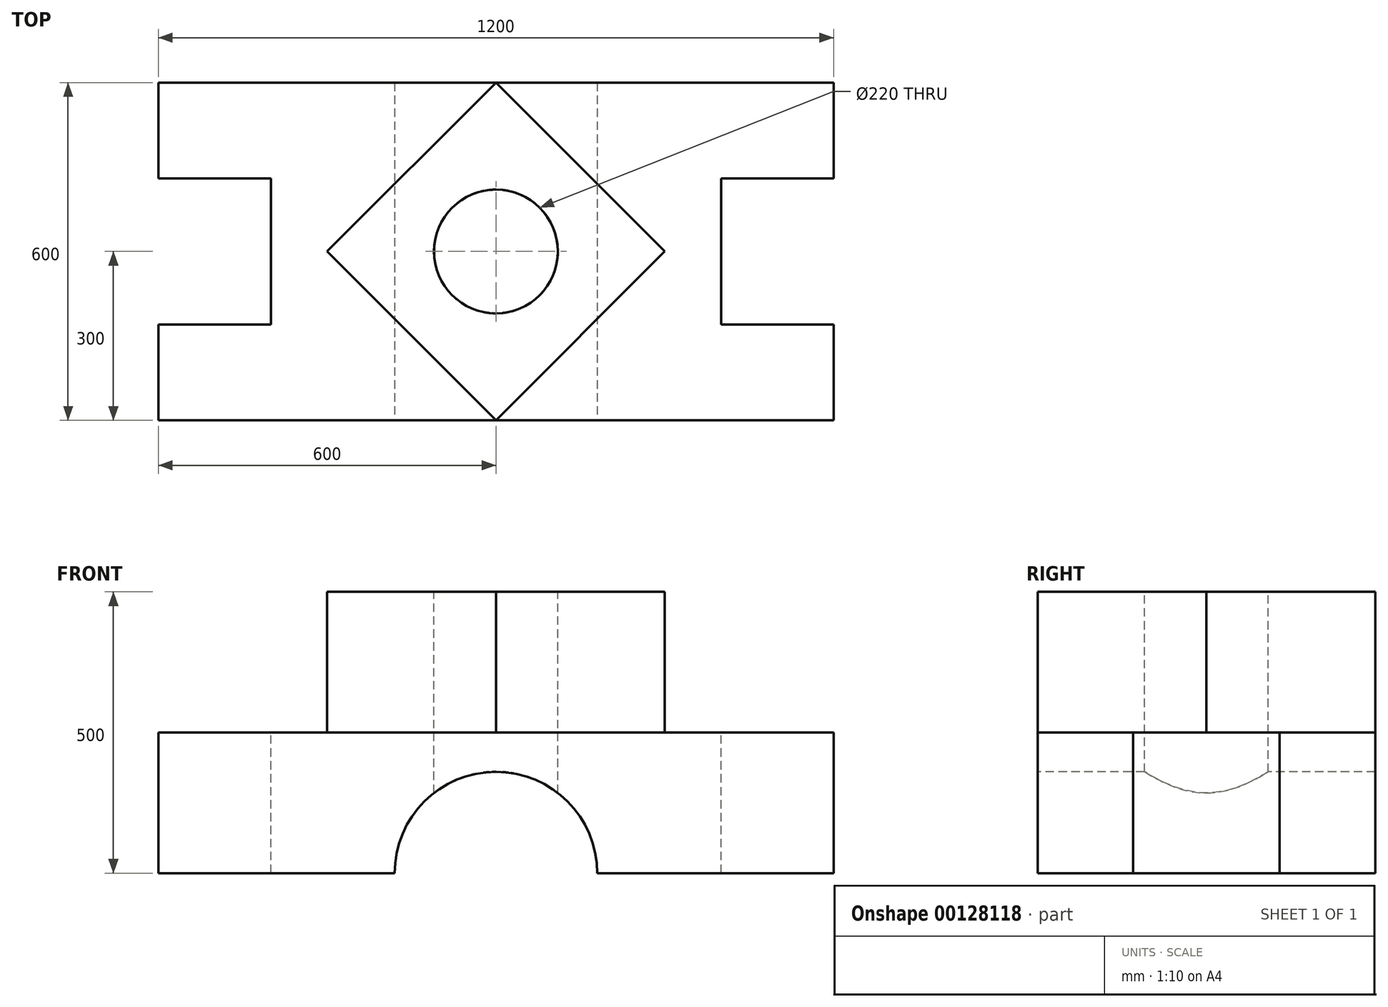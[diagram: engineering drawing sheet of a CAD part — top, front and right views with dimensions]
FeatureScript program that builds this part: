
annotation { "Feature Type Name" : "Feature", "Feature Type Description" : "" }
export const myFeature = defineFeature(function(context is Context, id is Id, definition is map)
    precondition{}
    {
        {
            var Q0;
            Q0=qCreatedBy(makeId("Top.planeOp"),FACE);
            var sketch = newSketch(context, id + "F0", { "sketchPlane" : qUnion([Q0])});
            skLineSegment(sketch, "E0.bottom", {"start": v(600, -300) * mm, "end": v(-600, -300) * mm});
            skLineSegment(sketch, "E0.top", {"start": v(600, 300) * mm, "end": v(-600, 300) * mm});
            skLineSegment(sketch, "E0.left", {"start": v(600, -300) * mm, "end": v(600, 300) * mm});
            skLineSegment(sketch, "E0.right", {"start": v(-600, -300) * mm, "end": v(-600, 300) * mm});
            skPoint(sketch, "E0.middle", {"position": v(0, 0) * mm});
            skSolve(sketch);
        }
        {
            var Q0;
            Q0 = qSketchRegion(id + "F0", true);
            extrude(context, id + "F1", {"entities" : qUnion([Q0]), "depth" : 250 * mm});
        }
        {
            var Q0;
            Q0=makeQuery(id+"F1.opExtrude","CAP_FACE",FACE,{"disambiguationData":[OSD([sQuery(id+"F0.wireOp",EDGE,"E0.bottom"),sQuery(id+"F0.wireOp",EDGE,"E0.top"),sQuery(id+"F0.wireOp",EDGE,"E0.left"),sQuery(id+"F0.wireOp",EDGE,"E0.right")])],"isStart":false});
            var sketch = newSketch(context, id + "F2", { "sketchPlane" : qUnion([Q0])});
            skPoint(sketch, "E1.middle", {"position": v(600, 0) * mm});
            skPoint(sketch, "E2.middle", {"position": v(-600, 0) * mm});
            skLineSegment(sketch, "E3.bottom", {"start": v(-400, -130) * mm, "end": v(-800, -130) * mm});
            skLineSegment(sketch, "E3.top", {"start": v(-400, 130) * mm, "end": v(-800, 130) * mm});
            skLineSegment(sketch, "E3.left", {"start": v(-400, -130) * mm, "end": v(-400, 130) * mm});
            skLineSegment(sketch, "E3.right", {"start": v(-800, -130) * mm, "end": v(-800, 130) * mm});
            skLineSegment(sketch, "E4.bottom", {"start": v(400, -130) * mm, "end": v(800, -130) * mm});
            skLineSegment(sketch, "E4.top", {"start": v(400, 130) * mm, "end": v(800, 130) * mm});
            skLineSegment(sketch, "E4.left", {"start": v(400, -130) * mm, "end": v(400, 130) * mm});
            skLineSegment(sketch, "E4.right", {"start": v(800, -130) * mm, "end": v(800, 130) * mm});
            skSolve(sketch);
        }
        {
            var Q0;
            Q0 = qSketchRegion(id + "F2", true);
            var Q1;
            {var subQ0=sQuery(id+"F2.wireOp",EDGE,"E2.bottom");Q1=makeQuery(id+"F2.imprint","IMPRINT",FACE,{"disambiguationData":[TD([[makeQuery(id+"F2.imprint","IMPRINT",EDGE,{"derivedFrom":subQ0}),-1.0]])]});}
            var Q2;
            {var subQ0=sQuery(id+"F2.wireOp",EDGE,"E1.bottom");Q2=makeQuery(id+"F2.imprint","IMPRINT",FACE,{"disambiguationData":[TD([[makeQuery(id+"F2.imprint","IMPRINT",EDGE,{"derivedFrom":subQ0}),1.0]])]});}
            extrude(context, id + "F3", {"entities" : qUnion([Q0, Q1, Q2]), "operationType" : NewBodyOperationType.REMOVE, "endBound" : BoundingType.THROUGH_ALL, "oppositeDirection" : true, "depth" : 25 * mm});
        }
        {
            var Q0;
            Q0=makeQuery(id+"F1.opExtrude","SWEPT_FACE",FACE,{"disambiguationData":[OSD([sQuery(id+"F0.wireOp",EDGE,"E0.bottom")])]});
            var sketch = newSketch(context, id + "F4", { "sketchPlane" : qUnion([Q0])});
            skArc(sketch, "E5", {"start": v(180, 0) * mm, "mid": v(0, 180) * mm, "end": v(-180, 0) * mm});
            skLineSegment(sketch, "E6", {"start": v(-180, 0) * mm, "end": v(180, 0) * mm});
            skSolve(sketch);
        }
        {
            var Q0;
            Q0=makeQuery(id+"F4.imprint","IMPRINT",FACE,{"disambiguationData":[TD([[makeQuery(id+"F4.imprint","IMPRINT",EDGE,{"derivedFrom":sQuery(id+"F4.wireOp",EDGE,"E5")}),1.0]])]});
            extrude(context, id + "F5", {"entities" : qUnion([Q0]), "operationType" : NewBodyOperationType.REMOVE, "endBound" : BoundingType.THROUGH_ALL, "oppositeDirection" : true, "depth" : 25 * mm});
        }
        {
            var Q0;
            Q0=makeQuery(id+"F1.opExtrude","CAP_FACE",FACE,{"disambiguationData":[OSD([sQuery(id+"F0.wireOp",EDGE,"E0.bottom"),sQuery(id+"F0.wireOp",EDGE,"E0.top"),sQuery(id+"F0.wireOp",EDGE,"E0.left"),sQuery(id+"F0.wireOp",EDGE,"E0.right")])],"isStart":false});
            var sketch = newSketch(context, id + "F6", { "sketchPlane" : qUnion([Q0])});
            skLineSegment(sketch, "E7", {"start": v(0, 300) * mm, "end": v(300, 0) * mm});
            skLineSegment(sketch, "E8", {"start": v(300, 0) * mm, "end": v(0, -300) * mm});
            skLineSegment(sketch, "E9", {"start": v(0, -300) * mm, "end": v(-300, 0) * mm});
            skLineSegment(sketch, "E10", {"start": v(-300, 0) * mm, "end": v(0, 300) * mm});
            skSolve(sketch);
        }
        {
            var Q0;
            Q0 = qSketchRegion(id + "F6", true);
            extrude(context, id + "F7", {"entities" : qUnion([Q0]), "operationType" : NewBodyOperationType.ADD, "depth" : 250 * mm});
        }
        {
            var Q0;
            Q0=makeQuery(id+"F7.opExtrude","CAP_FACE",FACE,{"disambiguationData":[OSD([sQuery(id+"F6.wireOp",EDGE,"E7"),sQuery(id+"F6.wireOp",EDGE,"E8"),sQuery(id+"F6.wireOp",EDGE,"E9"),sQuery(id+"F6.wireOp",EDGE,"E10")])],"isStart":false});
            var sketch = newSketch(context, id + "F8", { "sketchPlane" : qUnion([Q0])});
            skCircle(sketch, "E11", {"center": v(0, 0) * mm, "radius": 110 * mm});
            skSolve(sketch);
        }
        {
            var Q0;
            Q0 = qSketchRegion(id + "F8", true);
            extrude(context, id + "F9", {"entities" : qUnion([Q0]), "operationType" : NewBodyOperationType.REMOVE, "endBound" : BoundingType.THROUGH_ALL, "oppositeDirection" : true, "depth" : 25 * mm});
        }
    });
